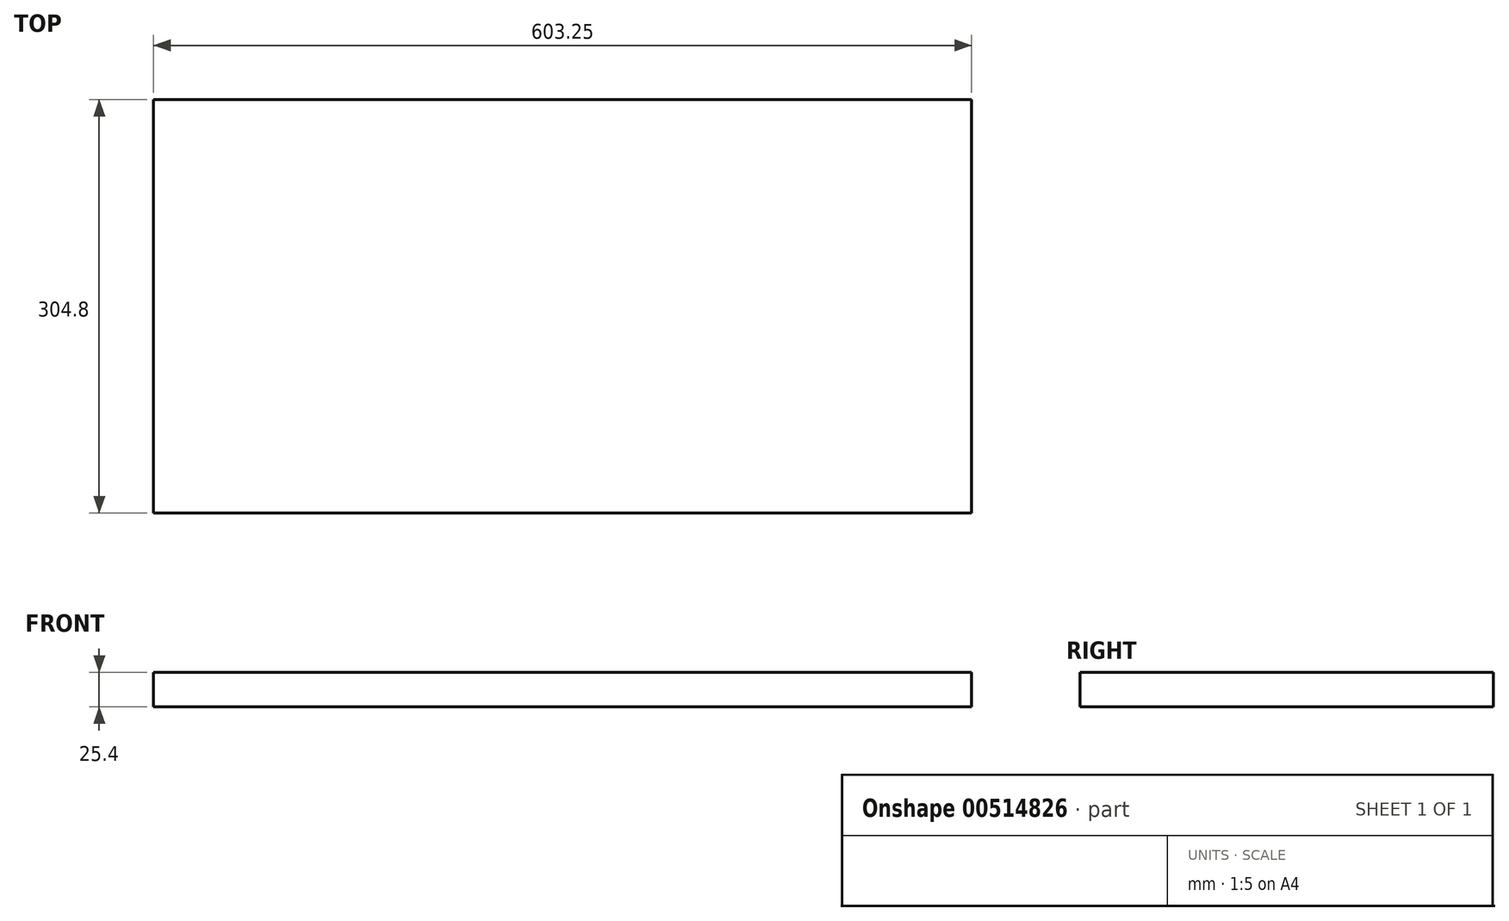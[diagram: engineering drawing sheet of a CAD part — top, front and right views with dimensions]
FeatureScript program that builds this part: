
annotation { "Feature Type Name" : "Feature", "Feature Type Description" : "" }
export const myFeature = defineFeature(function(context is Context, id is Id, definition is map)
    precondition{}
    {
        {
            var Q0;
            Q0=qCreatedBy(makeId("Front.planeOp"),FACE);
            var sketch = newSketch(context, id + "F0", { "sketchPlane" : qUnion([Q0])});
            skLineSegment(sketch, "E0.bottom", {"start": v(0, 0) * mm, "end": v(603.25, 0) * mm});
            skLineSegment(sketch, "E0.top", {"start": v(0, 25.4) * mm, "end": v(603.25, 25.4) * mm});
            skLineSegment(sketch, "E0.left", {"start": v(0, 0) * mm, "end": v(0, 25.4) * mm});
            skLineSegment(sketch, "E0.right", {"start": v(603.25, 0) * mm, "end": v(603.25, 25.4) * mm});
            skSolve(sketch);
        }
        {
            var Q0;
            Q0=makeQuery(id+"F0.imprint","IMPRINT",FACE,{"disambiguationData":[TD([[makeQuery(id+"F0.imprint","IMPRINT",EDGE,{"derivedFrom":sQuery(id+"F0.wireOp",EDGE,"E0.bottom")}),1.0]])]});
            extrude(context, id + "F1", {"entities" : qUnion([Q0]), "depth" : 304.8 * mm, "offsetDistance" : 25.4 * mm});
        }
    });
